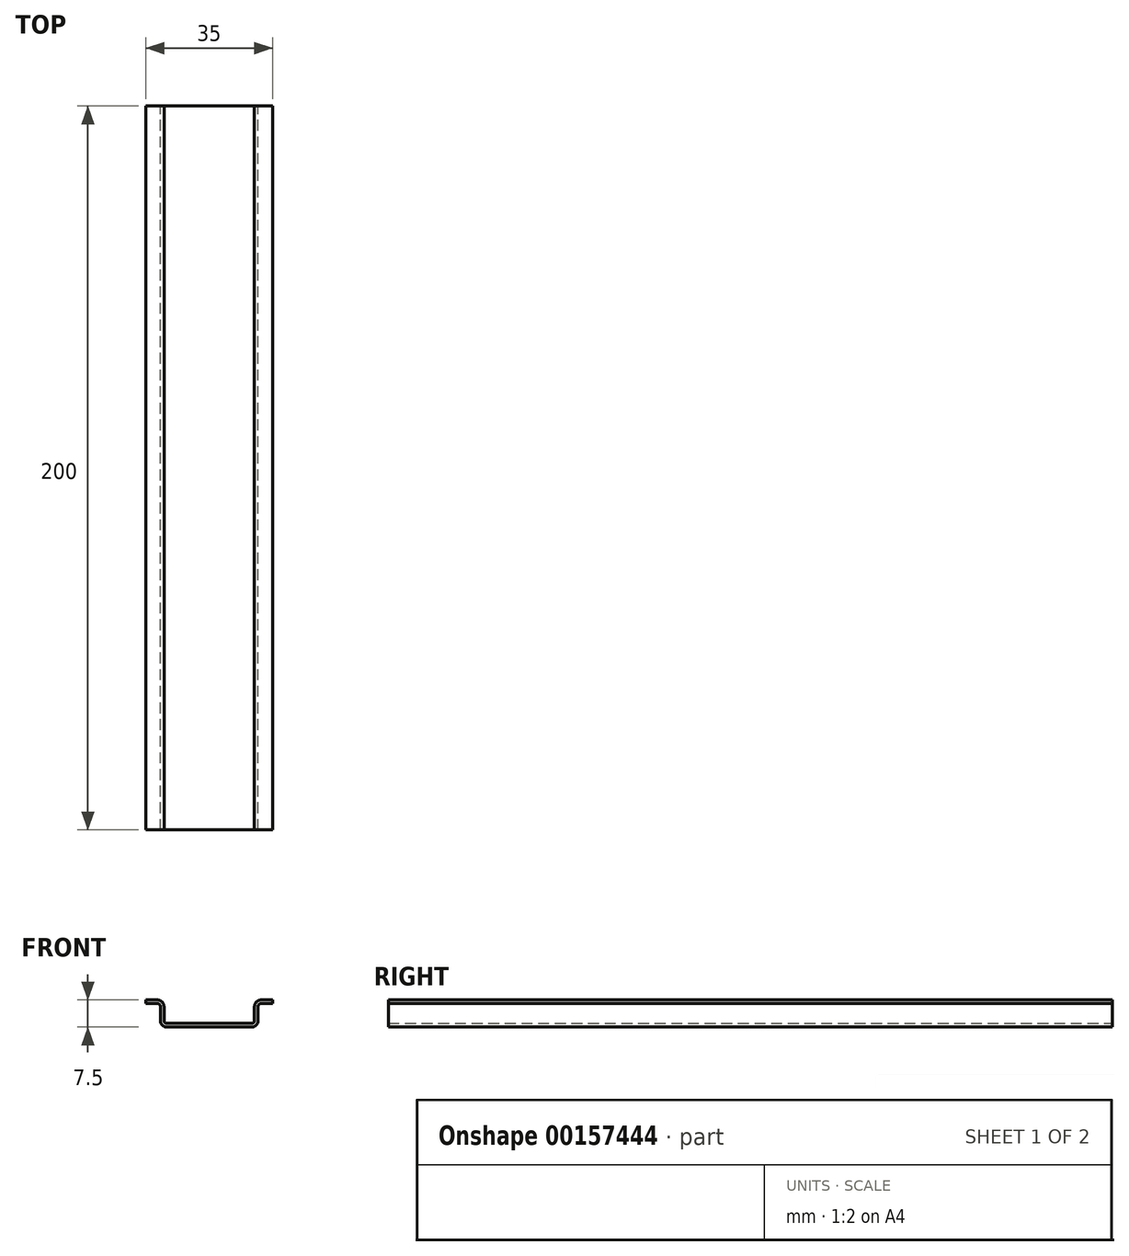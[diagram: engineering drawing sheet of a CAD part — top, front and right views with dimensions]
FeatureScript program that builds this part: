
annotation { "Feature Type Name" : "Feature", "Feature Type Description" : "" }
export const myFeature = defineFeature(function(context is Context, id is Id, definition is map)
    precondition{}
    {
        {
            var Q0;
            Q0=qCreatedBy(makeId("Front.planeOp"),FACE);
            var sketch = newSketch(context, id + "F0", { "sketchPlane" : qUnion([Q0])});
            skLineSegment(sketch, "E0", {"start": v(0, 0) * mm, "end": v(-23.4, 0) * mm});
            skArc(sketch, "E1", {"start": v(0, 0) * mm, "mid": v(1.27, 0.53) * mm, "end": v(1.8, 1.8) * mm});
            skArc(sketch, "E2", {"start": v(-23.4, 0) * mm, "mid": v(-24.67, 0.53) * mm, "end": v(-25.2, 1.8) * mm});
            skLineSegment(sketch, "E3", {"start": v(-25.2, 1.8) * mm, "end": v(-25.2, 5.7) * mm});
            skLineSegment(sketch, "E4", {"start": v(1.8, 1.8) * mm, "end": v(1.8, 5.7) * mm});
            skArc(sketch, "E5", {"start": v(-25.2, 5.7) * mm, "mid": v(-25.43, 6.27) * mm, "end": v(-26, 6.5) * mm});
            skArc(sketch, "E6", {"start": v(1.8, 5.7) * mm, "mid": v(2.03, 6.27) * mm, "end": v(2.6, 6.5) * mm});
            skLineSegment(sketch, "E7", {"start": v(-26, 6.5) * mm, "end": v(-29.2, 6.5) * mm});
            skLineSegment(sketch, "E8", {"start": v(2.6, 6.5) * mm, "end": v(5.8, 6.5) * mm});
            skLineSegment(sketch, "E9.0", {"start": v(-26, 7.5) * mm, "end": v(-29.2, 7.5) * mm});
            skArc(sketch, "E9.1", {"start": v(-24.2, 5.7) * mm, "mid": v(-24.73, 6.97) * mm, "end": v(-26, 7.5) * mm});
            skLineSegment(sketch, "E9.2", {"start": v(-24.2, 1.8) * mm, "end": v(-24.2, 5.7) * mm});
            skArc(sketch, "E9.3", {"start": v(-23.4, 1) * mm, "mid": v(-23.97, 1.23) * mm, "end": v(-24.2, 1.8) * mm});
            skLineSegment(sketch, "E9.4", {"start": v(0, 1) * mm, "end": v(-23.4, 1) * mm});
            skLineSegment(sketch, "E9.5", {"start": v(2.6, 7.5) * mm, "end": v(5.8, 7.5) * mm});
            skArc(sketch, "E9.6", {"start": v(0.8, 5.7) * mm, "mid": v(1.33, 6.97) * mm, "end": v(2.6, 7.5) * mm});
            skLineSegment(sketch, "E9.7", {"start": v(0.8, 1.8) * mm, "end": v(0.8, 5.7) * mm});
            skArc(sketch, "E9.8", {"start": v(0, 1) * mm, "mid": v(0.57, 1.23) * mm, "end": v(0.8, 1.8) * mm});
            skLineSegment(sketch, "E10", {"start": v(-29.2, 7.5) * mm, "end": v(-29.2, 6.5) * mm});
            skLineSegment(sketch, "E11", {"start": v(5.8, 7.5) * mm, "end": v(5.8, 6.5) * mm});
            skSolve(sketch);
        }
        {
            var Q0;
            Q0=makeQuery(id+"F0.imprint","IMPRINT",FACE,{"disambiguationData":[TD([[makeQuery(id+"F0.imprint","IMPRINT",EDGE,{"derivedFrom":sQuery(id+"F0.wireOp",EDGE,"E0")}),-1.0]])]});
            extrude(context, id + "F1", {"entities" : qUnion([Q0]), "depth" : 200 * mm});
        }
    });
